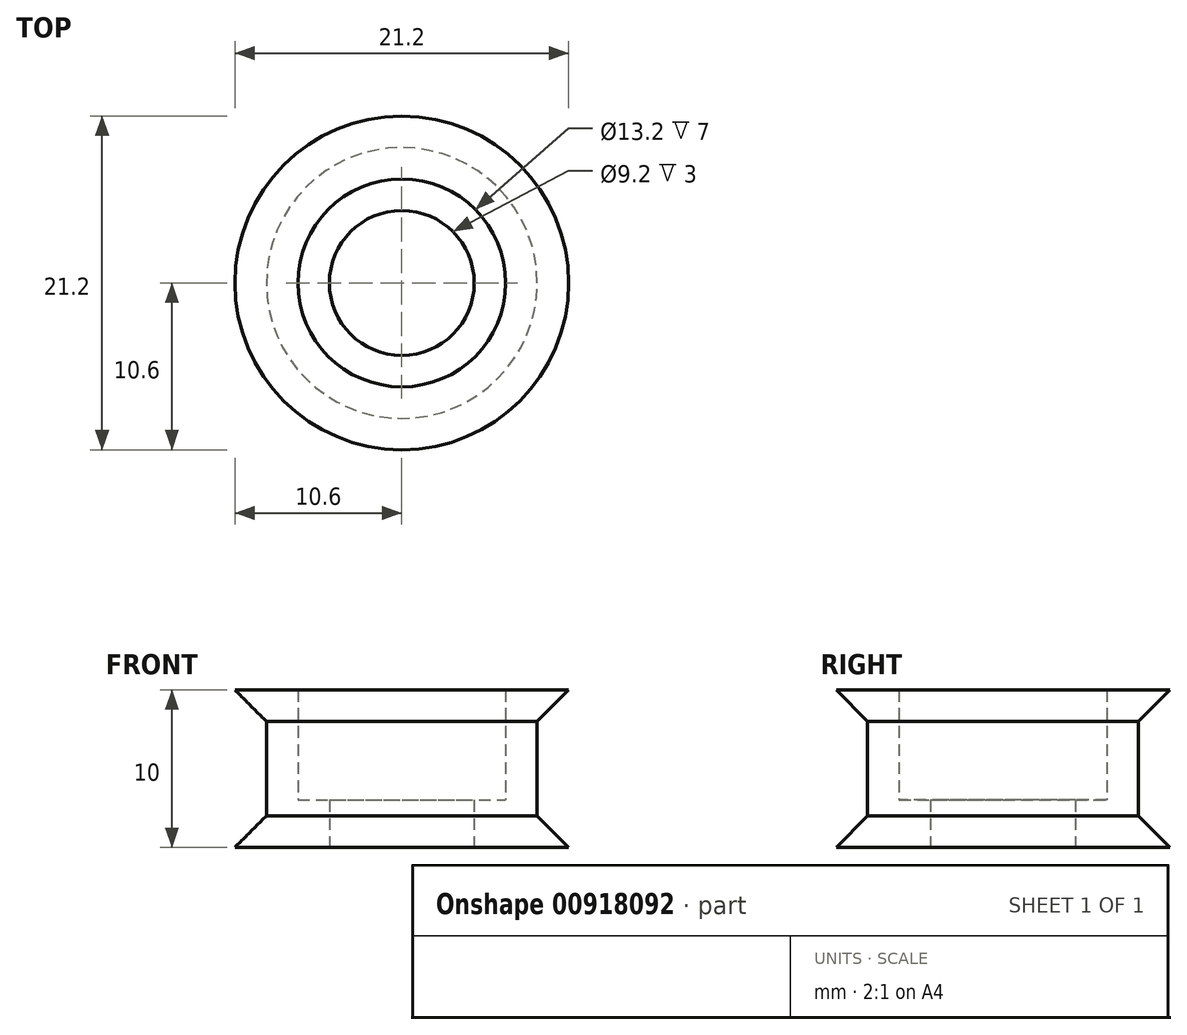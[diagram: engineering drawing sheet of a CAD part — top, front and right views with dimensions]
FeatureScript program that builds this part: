
annotation { "Feature Type Name" : "Feature", "Feature Type Description" : "" }
export const myFeature = defineFeature(function(context is Context, id is Id, definition is map)
    precondition{}
    {
        {
            var Q0;
            Q0=qCreatedBy(makeId("Front.planeOp"),FACE);
            var sketch = newSketch(context, id + "F0", { "sketchPlane" : qUnion([Q0])});
            skLineSegment(sketch, "E0", {"start": v(6.6, 4.8) * mm, "end": v(10.6, 4.8) * mm});
            skLineSegment(sketch, "E1", {"start": v(10.6, 4.8) * mm, "end": v(8.6, 2.8) * mm});
            skLineSegment(sketch, "E2", {"start": v(8.6, 2.8) * mm, "end": v(8.6, -3.2) * mm});
            skLineSegment(sketch, "E3", {"start": v(8.6, -3.2) * mm, "end": v(10.6, -5.2) * mm});
            skLineSegment(sketch, "E4", {"start": v(10.6, -5.2) * mm, "end": v(6.6, -5.2) * mm});
            skLineSegment(sketch, "E5", {"start": v(6.6, -5.2) * mm, "end": v(6.6, 4.8) * mm});
            skLineSegment(sketch, "E6", {"start": v(0, -3.77) * mm, "end": v(0, 4.95) * mm, "construction": true});
            skLineSegment(sketch, "E7.bottom", {"start": v(6.6, -5.2) * mm, "end": v(4.6, -5.2) * mm});
            skLineSegment(sketch, "E7.left", {"start": v(6.6, -5.2) * mm, "end": v(6.6, -3.7) * mm});
            skLineSegment(sketch, "E8", {"start": v(8.6, 2.8) * mm, "end": v(6.6, 2.8) * mm});
            skLineSegment(sketch, "E9", {"start": v(4.6, -2.2) * mm, "end": v(6.6, -2.2) * mm});
            skLineSegment(sketch, "E10", {"start": v(4.6, -5.2) * mm, "end": v(4.6, -2.2) * mm});
            skLineSegment(sketch, "E11", {"start": v(4.6, -2.2) * mm, "end": v(0, -2.2) * mm});
            skSolve(sketch);
        }
        {
            var Q0;
            Q0=qSketchRegion(id+"F0",true);
            var Q1;
            Q1=sQuery(id+"F0.wireOp",EDGE,"E6");
            revolve(context, id + "F1", {"entities" : qUnion([Q0]), "axis" : qUnion([Q1]), "revolveType" : RevolveType.FULL});
        }
    });
